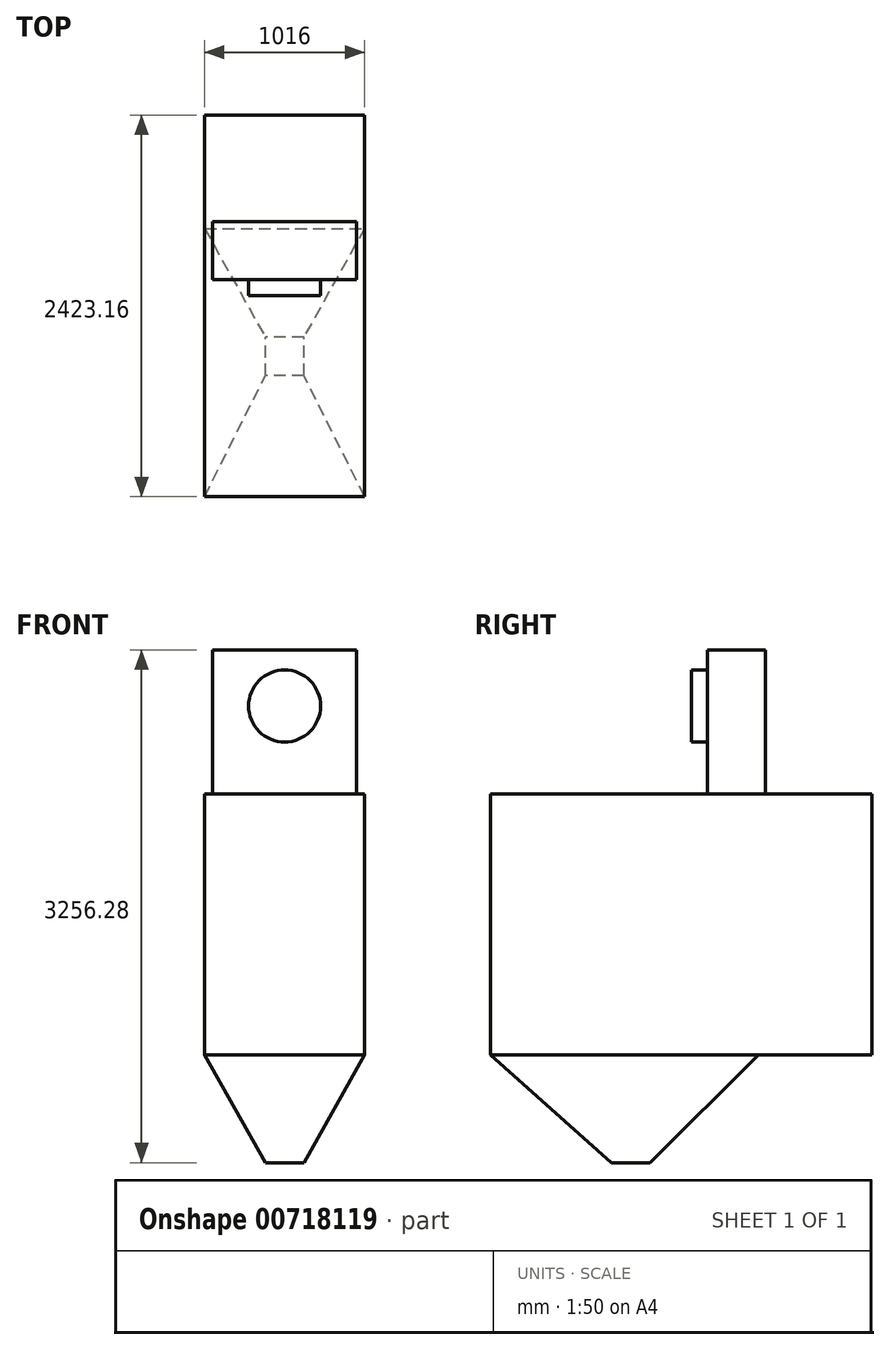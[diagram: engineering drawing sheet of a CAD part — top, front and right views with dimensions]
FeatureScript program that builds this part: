
annotation { "Feature Type Name" : "Feature", "Feature Type Description" : "" }
export const myFeature = defineFeature(function(context is Context, id is Id, definition is map)
    precondition{}
    {
        {
            var Q0;
            Q0=qCreatedBy(makeId("Top.planeOp"),FACE);
            var sketch = newSketch(context, id + "F0", { "sketchPlane" : qUnion([Q0])});
            skLineSegment(sketch, "E0.bottom", {"start": v(0, 0) * mm, "end": v(1016, 0) * mm});
            skLineSegment(sketch, "E0.top", {"start": v(0, 2423.16) * mm, "end": v(1016, 2423.16) * mm});
            skLineSegment(sketch, "E0.left", {"start": v(0, 0) * mm, "end": v(0, 2423.16) * mm});
            skLineSegment(sketch, "E0.right", {"start": v(1016, 0) * mm, "end": v(1016, 2423.16) * mm});
            skSolve(sketch);
        }
        {
            var Q0;
            Q0=makeQuery(id+"F0.imprint","IMPRINT",FACE,{"disambiguationData":[TD([[makeQuery(id+"F0.imprint","IMPRINT",EDGE,{"derivedFrom":sQuery(id+"F0.wireOp",EDGE,"E0.bottom")}),1.0]])]});
            extrude(context, id + "F1", {"entities" : qUnion([Q0]), "depth" : 1656.08 * mm, "offsetDistance" : 25.4 * mm});
        }
        {
            var Q0;
            Q0=makeQuery(id+"F1.opExtrude","CAP_FACE",FACE,{"disambiguationData":[OSD([sQuery(id+"F0.wireOp",EDGE,"E0.bottom"),sQuery(id+"F0.wireOp",EDGE,"E0.top"),sQuery(id+"F0.wireOp",EDGE,"E0.left"),sQuery(id+"F0.wireOp",EDGE,"E0.right")])],"isStart":false});
            var sketch = newSketch(context, id + "F2", { "sketchPlane" : qUnion([Q0])});
            skLineSegment(sketch, "E1", {"start": v(508, 0) * mm, "end": v(508, 1562.1) * mm, "construction": true});
            skLineSegment(sketch, "E2.bottom", {"start": v(965.2, 1744.98) * mm, "end": v(50.8, 1744.98) * mm});
            skLineSegment(sketch, "E2.top", {"start": v(965.2, 1379.22) * mm, "end": v(50.8, 1379.22) * mm});
            skLineSegment(sketch, "E2.left", {"start": v(965.2, 1744.98) * mm, "end": v(965.2, 1379.22) * mm});
            skLineSegment(sketch, "E2.right", {"start": v(50.8, 1744.98) * mm, "end": v(50.8, 1379.22) * mm});
            skPoint(sketch, "E2.middle", {"position": v(508, 1562.1) * mm});
            skSolve(sketch);
        }
        {
            var Q0;
            Q0 = qSketchRegion(id + "F2", true);
            extrude(context, id + "F3", {"entities" : qUnion([Q0]), "operationType" : NewBodyOperationType.ADD, "depth" : 914.4 * mm, "offsetDistance" : 25.4 * mm});
        }
        {
            var Q0;
            Q0=makeQuery(id+"F3.opExtrude","SWEPT_FACE",FACE,{"disambiguationData":[OSD([sQuery(id+"F2.wireOp",EDGE,"E2.top")])]});
            var sketch = newSketch(context, id + "F4", { "sketchPlane" : qUnion([Q0])});
            skLineSegment(sketch, "E3", {"start": v(508, 2570.48) * mm, "end": v(508, 2214.88) * mm, "construction": true});
            skCircle(sketch, "E4", {"center": v(508, 2214.88) * mm, "radius": 228.6 * mm});
            skSolve(sketch);
        }
        {
            var Q0;
            Q0 = qSketchRegion(id + "F4", true);
            extrude(context, id + "F5", {"entities" : qUnion([Q0]), "operationType" : NewBodyOperationType.ADD, "depth" : 101.6 * mm, "offsetDistance" : 25.4 * mm});
        }
        {
            var Q0;
            Q0=qCreatedBy(makeId("Top.planeOp"),FACE);
            cPlane(context, id + "F6", {"entities" : qUnion([Q0]), "cplaneType" : CPlaneType.OFFSET, "offset" : 685.8 * mm, "oppositeDirection" : true, "width" : 152.4 * mm, "height" : 152.4 * mm});
        }
        {
            var Q0;
            Q0=makeQuery(id+"F1.opExtrude","CAP_FACE",FACE,{"disambiguationData":[OSD([sQuery(id+"F0.wireOp",EDGE,"E0.bottom"),sQuery(id+"F0.wireOp",EDGE,"E0.top"),sQuery(id+"F0.wireOp",EDGE,"E0.left"),sQuery(id+"F0.wireOp",EDGE,"E0.right")])],"isStart":true});
            var sketch = newSketch(context, id + "F7", { "sketchPlane" : qUnion([Q0])});
            skLineSegment(sketch, "E5.bottom", {"start": v(0, 0) * mm, "end": v(1016, 0) * mm});
            skLineSegment(sketch, "E5.top", {"start": v(0, -1701.8) * mm, "end": v(1016, -1701.8) * mm});
            skLineSegment(sketch, "E5.left", {"start": v(0, 0) * mm, "end": v(0, -1701.8) * mm});
            skLineSegment(sketch, "E5.right", {"start": v(1016, 0) * mm, "end": v(1016, -1701.8) * mm});
            skSolve(sketch);
        }
        {
            var Q0;
            Q0=qCreatedBy(id+"F6.planeOp",FACE);
            var sketch = newSketch(context, id + "F8", { "sketchPlane" : qUnion([Q0])});
            skLineSegment(sketch, "E6", {"start": v(0, 39.54) * mm, "end": v(508, 39.54) * mm, "construction": true});
            skLineSegment(sketch, "E7", {"start": v(508, 39.54) * mm, "end": v(508, 890.44) * mm, "construction": true});
            skLineSegment(sketch, "E8.bottom", {"start": v(629.92, 768.52) * mm, "end": v(386.08, 768.52) * mm});
            skLineSegment(sketch, "E8.top", {"start": v(629.92, 1012.36) * mm, "end": v(386.08, 1012.36) * mm});
            skLineSegment(sketch, "E8.left", {"start": v(629.92, 768.52) * mm, "end": v(629.92, 1012.36) * mm});
            skLineSegment(sketch, "E8.right", {"start": v(386.08, 768.52) * mm, "end": v(386.08, 1012.36) * mm});
            skPoint(sketch, "E8.middle", {"position": v(508, 890.44) * mm});
            skSolve(sketch);
        }
        {
            var Q1;
            Q1=makeQuery(id+"F7.imprint","IMPRINT",FACE,{"disambiguationData":[TD([[makeQuery(id+"F7.imprint","IMPRINT",EDGE,{"derivedFrom":sQuery(id+"F7.wireOp",EDGE,"E5.bottom")}),-1.0]])]});
            var Q2;
            Q2=makeQuery(id+"F8.imprint","IMPRINT",FACE,{"disambiguationData":[TD([[makeQuery(id+"F8.imprint","IMPRINT",EDGE,{"derivedFrom":sQuery(id+"F8.wireOp",EDGE,"E8.bottom")}),-1.0]])]});
            loft(context, id + "F9", {"operationType" : NewBodyOperationType.ADD, "sheetProfilesArray" : [{ "sheetProfileEntities" : qUnion([Q1]) }, { "sheetProfileEntities" : qUnion([Q2]) }]});
        }
    });
